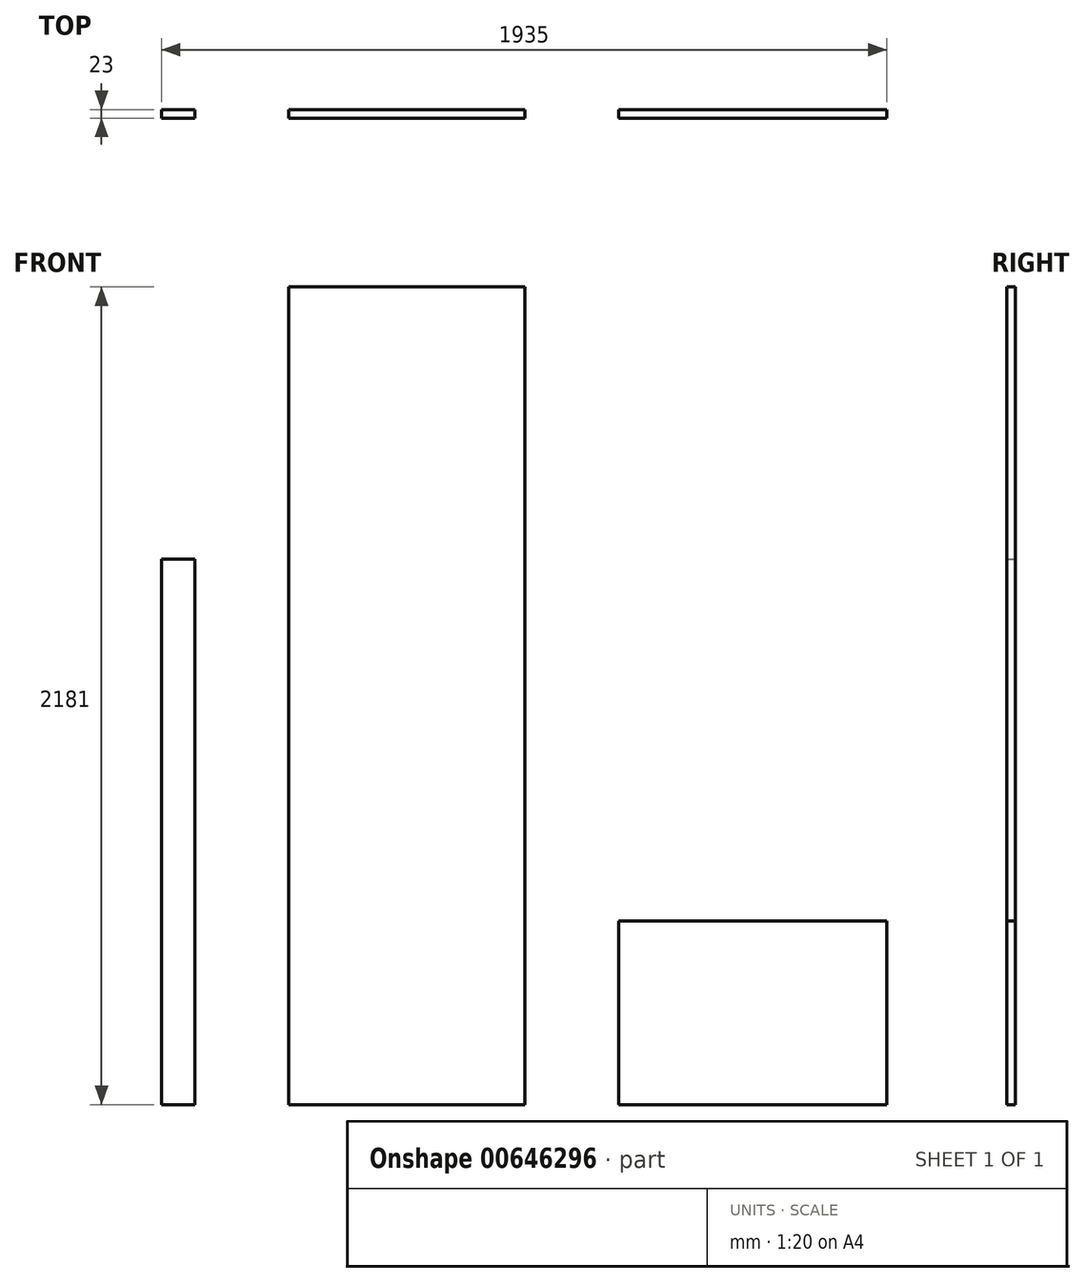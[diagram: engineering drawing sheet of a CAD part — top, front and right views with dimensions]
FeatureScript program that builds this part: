
annotation { "Feature Type Name" : "Feature", "Feature Type Description" : "" }
export const myFeature = defineFeature(function(context is Context, id is Id, definition is map)
    precondition{}
    {
        {
            var Q0;
            Q0=qCreatedBy(makeId("Front.planeOp"),FACE);
            var sketch = newSketch(context, id + "F0", { "sketchPlane" : qUnion([Q0])});
            skLineSegment(sketch, "E0.bottom", {"start": v(0, 0) * mm, "end": v(716, 0) * mm});
            skLineSegment(sketch, "E0.top", {"start": v(0, 490) * mm, "end": v(716, 490) * mm});
            skLineSegment(sketch, "E0.left", {"start": v(0, 0) * mm, "end": v(0, 490) * mm});
            skLineSegment(sketch, "E0.right", {"start": v(716, 0) * mm, "end": v(716, 490) * mm});
            skSolve(sketch);
        }
        {
            var Q0;
            Q0 = qSketchRegion(id + "F0", true);
            extrude(context, id + "F1", {"entities" : qUnion([Q0]), "depth" : 23 * mm, "offsetDistance" : 25 * mm});
        }
        {
            var Q0;
            Q0=qCreatedBy(makeId("Front.planeOp"),FACE);
            var sketch = newSketch(context, id + "F2", { "sketchPlane" : qUnion([Q0])});
            skLineSegment(sketch, "E1.bottom", {"start": v(-250, 0) * mm, "end": v(-880, 0) * mm});
            skLineSegment(sketch, "E1.top", {"start": v(-250, 2181) * mm, "end": v(-880, 2181) * mm});
            skLineSegment(sketch, "E1.left", {"start": v(-250, 0) * mm, "end": v(-250, 2181) * mm});
            skLineSegment(sketch, "E1.right", {"start": v(-880, 0) * mm, "end": v(-880, 2181) * mm});
            skSolve(sketch);
        }
        {
            var Q0;
            Q0=makeQuery(id+"F2.imprint","IMPRINT",FACE,{"disambiguationData":[TD([[makeQuery(id+"F2.imprint","IMPRINT",EDGE,{"derivedFrom":sQuery(id+"F2.wireOp",EDGE,"E1.bottom")}),-1.0]])]});
            extrude(context, id + "F3", {"entities" : qUnion([Q0]), "depth" : 23 * mm, "offsetDistance" : 25 * mm});
        }
        {
            var Q0;
            Q0=qCreatedBy(makeId("Front.planeOp"),FACE);
            var sketch = newSketch(context, id + "F4", { "sketchPlane" : qUnion([Q0])});
            skLineSegment(sketch, "E2.bottom", {"start": v(-1130, 0) * mm, "end": v(-1219, 0) * mm});
            skLineSegment(sketch, "E2.top", {"start": v(-1130, 1455) * mm, "end": v(-1219, 1455) * mm});
            skLineSegment(sketch, "E2.left", {"start": v(-1130, 0) * mm, "end": v(-1130, 1455) * mm});
            skLineSegment(sketch, "E2.right", {"start": v(-1219, 0) * mm, "end": v(-1219, 1455) * mm});
            skSolve(sketch);
        }
        {
            var Q0;
            Q0 = qSketchRegion(id + "F4", true);
            extrude(context, id + "F5", {"entities" : qUnion([Q0]), "depth" : 23 * mm, "offsetDistance" : 25 * mm});
        }
    });
